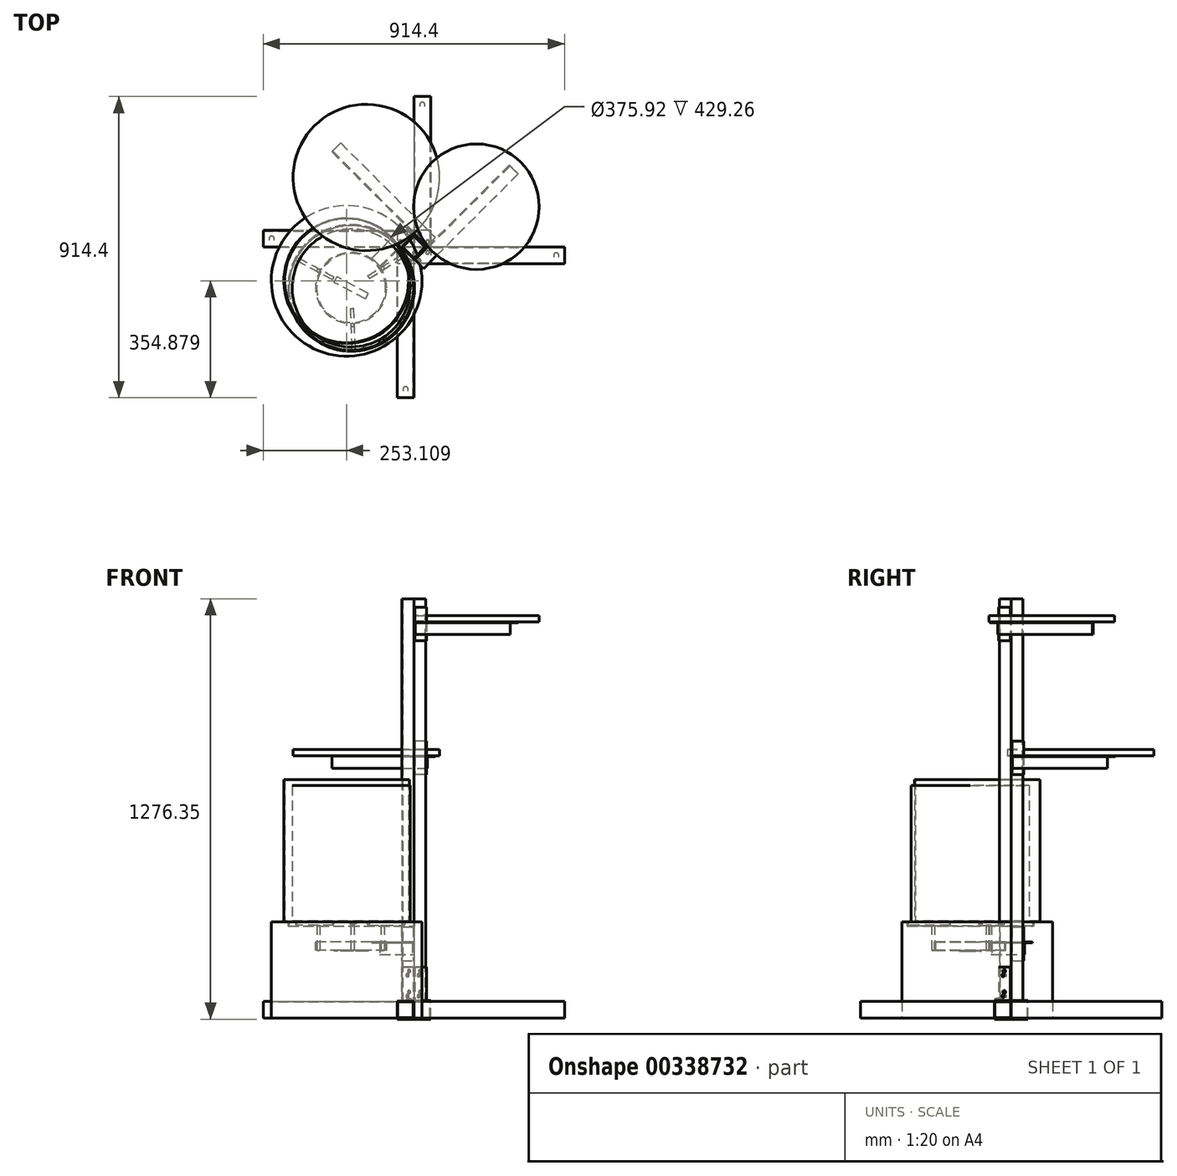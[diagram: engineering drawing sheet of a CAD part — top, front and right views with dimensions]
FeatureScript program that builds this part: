
annotation { "Feature Type Name" : "Feature", "Feature Type Description" : "" }
export const myFeature = defineFeature(function(context is Context, id is Id, definition is map)
    precondition{}
    {
        {
            var Q0;
            Q0=qCreatedBy(makeId("Front.planeOp"),FACE);
            var sketch = newSketch(context, id + "F0", { "sketchPlane" : qUnion([Q0])});
            skLineSegment(sketch, "E0.bottom", {"start": v(0, 0) * mm, "end": v(50.8, 0) * mm});
            skLineSegment(sketch, "E0.top", {"start": v(0, 50.8) * mm, "end": v(50.8, 50.8) * mm});
            skLineSegment(sketch, "E0.left", {"start": v(0, 0) * mm, "end": v(0, 50.8) * mm});
            skLineSegment(sketch, "E0.right", {"start": v(50.8, 0) * mm, "end": v(50.8, 50.8) * mm});
            skLineSegment(sketch, "E1.0", {"start": v(49.15, 1.65) * mm, "end": v(49.15, 49.15) * mm});
            skLineSegment(sketch, "E2.0", {"start": v(1.65, 49.15) * mm, "end": v(49.15, 49.15) * mm});
            skLineSegment(sketch, "E3.0", {"start": v(1.65, 1.65) * mm, "end": v(1.65, 49.15) * mm});
            skLineSegment(sketch, "E4.0", {"start": v(1.65, 1.65) * mm, "end": v(49.15, 1.65) * mm});
            skSolve(sketch);
        }
        {
            var Q0;
            Q0 = qSketchRegion(id + "F0", true);
            extrude(context, id + "F1", {"entities" : qUnion([Q0]), "oppositeDirection" : true, "depth" : 457.2 * mm});
        }
        {
            var Q0;
            Q0=makeQuery(id+"F1.opExtrude","SWEPT_FACE",FACE,{"disambiguationData":[OSD([sQuery(id+"F0.wireOp",EDGE,"E0.bottom")])]});
            var sketch = newSketch(context, id + "F2", { "sketchPlane" : qUnion([Q0])});
            skCircle(sketch, "E5", {"center": v(25.4, -431.8) * mm, "radius": 7.94 * mm});
            skSolve(sketch);
        }
        {
            var Q0;
            Q0=makeQuery(id+"F2.imprint","IMPRINT",FACE,{"disambiguationData":[TD([[makeQuery(id+"F2.imprint","IMPRINT",EDGE,{"derivedFrom":sQuery(id+"F2.wireOp",EDGE,"E5")}),1.0]])]});
            extrude(context, id + "F3", {"entities" : qUnion([Q0]), "operationType" : NewBodyOperationType.REMOVE, "endBound" : BoundingType.UP_TO_NEXT, "oppositeDirection" : true, "depth" : 25.4 * mm});
        }
        {
            var Q0;
            Q0=makeQuery(id+"F1.opExtrude","SWEPT_FACE",FACE,{"disambiguationData":[OSD([sQuery(id+"F0.wireOp",EDGE,"E0.top")])]});
            var sketch = newSketch(context, id + "F4", { "sketchPlane" : qUnion([Q0])});
            skLineSegment(sketch, "E6.bottom", {"start": v(50.8, 50.8) * mm, "end": v(-50.8, 50.8) * mm});
            skLineSegment(sketch, "E6.top", {"start": v(50.8, -50.8) * mm, "end": v(-50.8, -50.8) * mm});
            skLineSegment(sketch, "E6.left", {"start": v(50.8, 50.8) * mm, "end": v(50.8, -50.8) * mm});
            skLineSegment(sketch, "E6.right", {"start": v(-50.8, 50.8) * mm, "end": v(-50.8, -50.8) * mm});
            skSolve(sketch);
        }
        {
            var Q0;
            Q0 = qSketchRegion(id + "F4", true);
            extrude(context, id + "F5", {"entities" : qUnion([Q0]), "depth" : 3.17 * mm});
        }
        {
            var Q0;
            Q0=makeQuery(id+"F5.opExtrude","CAP_FACE",FACE,{"disambiguationData":[OSD([sQuery(id+"F4.wireOp",EDGE,"E6.bottom"),sQuery(id+"F4.wireOp",EDGE,"E6.top"),sQuery(id+"F4.wireOp",EDGE,"E6.left"),sQuery(id+"F4.wireOp",EDGE,"E6.right")])],"isStart":false});
            var sketch = newSketch(context, id + "F6", { "sketchPlane" : qUnion([Q0])});
            skLineSegment(sketch, "E7", {"start": v(-50.8, -50.8) * mm, "end": v(50.8, 50.8) * mm, "construction": true});
            skLineSegment(sketch, "E8", {"start": v(0, 0) * mm, "end": v(0, -50.8) * mm, "construction": true});
            skLineSegment(sketch, "E9", {"start": v(2.25, -38.17) * mm, "end": v(38.17, -2.25) * mm});
            skLineSegment(sketch, "E10", {"start": v(38.17, -2.25) * mm, "end": v(35.92, 0) * mm});
            skLineSegment(sketch, "E11", {"start": v(35.92, 0) * mm, "end": v(0, -35.92) * mm});
            skLineSegment(sketch, "E12", {"start": v(1.26, -37.19) * mm, "end": v(2.25, -38.17) * mm});
            skLineSegment(sketch, "E13", {"start": v(0, -35.92) * mm, "end": v(-35.92, 0) * mm});
            skLineSegment(sketch, "E14", {"start": v(-35.92, 0) * mm, "end": v(-38.17, -2.25) * mm});
            skLineSegment(sketch, "E15", {"start": v(-38.17, -2.25) * mm, "end": v(-2.19, -38.1) * mm});
            skLineSegment(sketch, "E16", {"start": v(-1.26, -37.19) * mm, "end": v(-2.19, -38.1) * mm});
            skArc(sketch, "E17", {"start": v(-1.26, -37.19) * mm, "mid": v(0, -37.7) * mm, "end": v(1.26, -37.19) * mm});
            skSolve(sketch);
        }
        {
            var Q0;
            Q0 = qSketchRegion(id + "F6", true);
            extrude(context, id + "F7", {"entities" : qUnion([Q0]), "depth" : 101.6 * mm});
        }
        {
            var Q0;
            Q0=makeQuery(id+"F5.opExtrude","CAP_FACE",FACE,{"disambiguationData":[OSD([sQuery(id+"F4.wireOp",EDGE,"E6.bottom"),sQuery(id+"F4.wireOp",EDGE,"E6.top"),sQuery(id+"F4.wireOp",EDGE,"E6.left"),sQuery(id+"F4.wireOp",EDGE,"E6.right")])],"isStart":false});
            var sketch = newSketch(context, id + "F8", { "sketchPlane" : qUnion([Q0])});
            skCircle(sketch, "E18", {"center": v(15.88, -41.27) * mm, "radius": 4.76 * mm});
            skCircle(sketch, "E19", {"center": v(41.28, -15.88) * mm, "radius": 4.76 * mm});
            skCircle(sketch, "E20.MirrorC", {"center": v(-15.88, -41.27) * mm, "radius": 4.76 * mm});
            skCircle(sketch, "E21.MirrorC", {"center": v(-41.28, -15.88) * mm, "radius": 4.76 * mm});
            skCircle(sketch, "E22.MirrorC", {"center": v(15.88, 41.27) * mm, "radius": 4.76 * mm});
            skCircle(sketch, "E23.MirrorC", {"center": v(41.28, 15.88) * mm, "radius": 4.76 * mm});
            skCircle(sketch, "E24.MirrorC", {"center": v(-15.88, 41.27) * mm, "radius": 4.76 * mm});
            skCircle(sketch, "E25.MirrorC", {"center": v(-41.28, 15.88) * mm, "radius": 4.76 * mm});
            skSolve(sketch);
        }
        {
            var Q0;
            Q0 = qSketchRegion(id + "F8", true);
            extrude(context, id + "F9", {"entities" : qUnion([Q0]), "operationType" : NewBodyOperationType.REMOVE, "oppositeDirection" : true, "depth" : 25.4 * mm});
        }
        {
            var Q0;
            Q0=makeQuery(id+"F1.opExtrude","SWEPT_FACE",FACE,{"disambiguationData":[OSD([sQuery(id+"F0.wireOp",EDGE,"E0.top")])]});
            var sketch = newSketch(context, id + "F10", { "sketchPlane" : qUnion([Q0])});
            skCircle(sketch, "E26.0", {"center": v(15.88, 41.27) * mm, "radius": 4.76 * mm, "construction": true});
            skCircle(sketch, "E27.0", {"center": v(41.28, 15.88) * mm, "radius": 4.76 * mm, "construction": true});
            skCircle(sketch, "E28", {"center": v(15.88, 41.27) * mm, "radius": 5.72 * mm});
            skCircle(sketch, "E29", {"center": v(41.28, 15.88) * mm, "radius": 5.72 * mm});
            skSolve(sketch);
        }
        {
            var Q0;
            Q0 = qSketchRegion(id + "F10", true);
            extrude(context, id + "F11", {"entities" : qUnion([Q0]), "operationType" : NewBodyOperationType.REMOVE, "endBound" : BoundingType.THROUGH_ALL, "oppositeDirection" : true, "depth" : 25.4 * mm});
        }
        {
            var Q0;
            Q0=makeQuery(id+"F1.opExtrude","SWEPT_BODY",BODY,{"disambiguationData":[OSD([sQuery(id+"F0.wireOp",EDGE,"E0.bottom"),sQuery(id+"F0.wireOp",EDGE,"E0.top"),sQuery(id+"F0.wireOp",EDGE,"E0.left"),sQuery(id+"F0.wireOp",EDGE,"E0.right"),sQuery(id+"F0.wireOp",EDGE,"E1.0"),sQuery(id+"F0.wireOp",EDGE,"E2.0"),sQuery(id+"F0.wireOp",EDGE,"E3.0"),sQuery(id+"F0.wireOp",EDGE,"E4.0")])]});
            var Q1;
            Q1=makeQuery(id+"F1.opExtrude","CAP_EDGE",EDGE,{"disambiguationData":[OSD([sQuery(id+"F0.wireOp",EDGE,"E0.left")])],"isStart":true});
            circularPattern(context, id + "F12", {"entities" : qUnion([Q0]), "axis" : qUnion([Q1]), "angle" : 360 * degree, "instanceCount" : 4, "equalSpace" : true});
        }
        {
            var Q0;
            Q0=qCreatedBy(makeId("Top.planeOp"),FACE);
            var sketch = newSketch(context, id + "F13", { "sketchPlane" : qUnion([Q0])});
            skLineSegment(sketch, "E30.0.0", {"start": v(50.8, -50.8) * mm, "end": v(50.8, 50.8) * mm});
            skLineSegment(sketch, "E30.0.1", {"start": v(50.8, 50.8) * mm, "end": v(-50.8, 50.8) * mm});
            skLineSegment(sketch, "E30.0.2", {"start": v(-50.8, 50.8) * mm, "end": v(-50.8, -50.8) * mm});
            skLineSegment(sketch, "E30.0.3", {"start": v(-50.8, -50.8) * mm, "end": v(50.8, -50.8) * mm});
            skCircle(sketch, "E31.0", {"center": v(41.28, -15.88) * mm, "radius": 4.76 * mm});
            skCircle(sketch, "E31.1", {"center": v(41.28, 15.88) * mm, "radius": 4.76 * mm});
            skCircle(sketch, "E31.2", {"center": v(15.88, -41.27) * mm, "radius": 4.76 * mm});
            skCircle(sketch, "E31.3", {"center": v(15.88, 41.27) * mm, "radius": 4.76 * mm});
            skCircle(sketch, "E31.4", {"center": v(-41.28, -15.88) * mm, "radius": 4.76 * mm});
            skCircle(sketch, "E31.5", {"center": v(-41.28, 15.88) * mm, "radius": 4.76 * mm});
            skCircle(sketch, "E31.6", {"center": v(-15.88, -41.27) * mm, "radius": 4.76 * mm});
            skCircle(sketch, "E31.7", {"center": v(-15.88, 41.27) * mm, "radius": 4.76 * mm});
            skSolve(sketch);
        }
        {
            var Q0;
            Q0 = qSketchRegion(id + "F13", true);
            extrude(context, id + "F14", {"entities" : qUnion([Q0]), "oppositeDirection" : true, "depth" : 3.17 * mm});
        }
        {
            var Q0;
            Q0=makeQuery(id+"F7.opExtrude","SWEPT_FACE",FACE,{"disambiguationData":[OSD([sQuery(id+"F6.wireOp",EDGE,"E9")])]});
            var sketch = newSketch(context, id + "F15", { "sketchPlane" : qUnion([Q0])});
            skLineSegment(sketch, "E32", {"start": v(-6.35, 176.29) * mm, "end": v(-6.35, 53.97) * mm, "construction": true});
            skLineSegment(sketch, "E33", {"start": v(0, 172.23) * mm, "end": v(0, 53.97) * mm, "construction": true});
            skCircle(sketch, "E34", {"center": v(-6.35, 66.67) * mm, "radius": 4.76 * mm});
            skCircle(sketch, "E35", {"center": v(0, 79.38) * mm, "radius": 4.76 * mm});
            skCircle(sketch, "E36", {"center": v(0, 142.88) * mm, "radius": 4.76 * mm});
            skCircle(sketch, "E37", {"center": v(-6.35, 130.18) * mm, "radius": 4.76 * mm});
            skSolve(sketch);
        }
        {
            var Q0;
            Q0 = qSketchRegion(id + "F15", true);
            extrude(context, id + "F16", {"entities" : qUnion([Q0]), "operationType" : NewBodyOperationType.REMOVE, "oppositeDirection" : true, "depth" : 25.4 * mm});
        }
        {
            var Q0;
            Q0=makeQuery(id+"F7.opExtrude","SWEPT_FACE",FACE,{"disambiguationData":[OSD([sQuery(id+"F6.wireOp",EDGE,"E15")])]});
            var sketch = newSketch(context, id + "F17", { "sketchPlane" : qUnion([Q0])});
            skLineSegment(sketch, "E38", {"start": v(6.3, 167.64) * mm, "end": v(6.3, 53.97) * mm, "construction": true});
            skPoint(sketch, "E39.endSnap0", {"position": v(-0.05, 53.97) * mm});
            skLineSegment(sketch, "E40", {"start": v(-0.05, 173.56) * mm, "end": v(-0.05, 53.97) * mm, "construction": true});
            skCircle(sketch, "E41", {"center": v(-0.05, 66.67) * mm, "radius": 4.76 * mm});
            skCircle(sketch, "E42", {"center": v(6.3, 79.38) * mm, "radius": 4.76 * mm});
            skCircle(sketch, "E43", {"center": v(6.3, 142.88) * mm, "radius": 4.76 * mm});
            skCircle(sketch, "E44", {"center": v(-0.05, 130.18) * mm, "radius": 4.76 * mm});
            skSolve(sketch);
        }
        {
            var Q0;
            Q0 = qSketchRegion(id + "F17", true);
            extrude(context, id + "F18", {"entities" : qUnion([Q0]), "operationType" : NewBodyOperationType.REMOVE, "oppositeDirection" : true, "depth" : 25.4 * mm});
        }
        {
            var Q0;
            Q0=makeQuery(id+"F5.opExtrude","CAP_FACE",FACE,{"disambiguationData":[OSD([sQuery(id+"F4.wireOp",EDGE,"E6.bottom"),sQuery(id+"F4.wireOp",EDGE,"E6.top"),sQuery(id+"F4.wireOp",EDGE,"E6.left"),sQuery(id+"F4.wireOp",EDGE,"E6.right")])],"isStart":false});
            var sketch = newSketch(context, id + "F19", { "sketchPlane" : qUnion([Q0])});
            skPoint(sketch, "E45.middle", {"position": v(0, 0) * mm});
            skLineSegment(sketch, "E46.0", {"start": v(35.92, 0) * mm, "end": v(0, -35.92) * mm});
            skLineSegment(sketch, "E46.1", {"start": v(0, -35.92) * mm, "end": v(-35.92, 0) * mm});
            skLineSegment(sketch, "E47", {"start": v(-35.92, 0) * mm, "end": v(0, 35.92) * mm});
            skLineSegment(sketch, "E48", {"start": v(0, 35.92) * mm, "end": v(35.92, 0) * mm});
            skLineSegment(sketch, "E49.0", {"start": v(-33.59, 0) * mm, "end": v(0, 33.59) * mm});
            skLineSegment(sketch, "E50.0", {"start": v(0, 33.59) * mm, "end": v(33.59, 0) * mm});
            skLineSegment(sketch, "E51.0", {"start": v(33.59, 0) * mm, "end": v(0, -33.59) * mm});
            skLineSegment(sketch, "E52.0", {"start": v(0, -33.59) * mm, "end": v(-33.59, 0) * mm});
            skSolve(sketch);
        }
        {
            var Q0;
            Q0 = qSketchRegion(id + "F19", true);
            extrude(context, id + "F20", {"entities" : qUnion([Q0]), "depth" : 1219.2 * mm});
        }
        {
            var Q0;
            Q0=makeQuery(id+"F20.opExtrude","SWEPT_FACE",FACE,{"disambiguationData":[OSD([sQuery(id+"F19.wireOp",EDGE,"E48")])]});
            var sketch = newSketch(context, id + "F21", { "sketchPlane" : qUnion([Q0])});
            skLineSegment(sketch, "E53.0", {"start": v(-25.4, 841.38) * mm, "end": v(-25.4, 739.78) * mm});
            skLineSegment(sketch, "E54.0", {"start": v(25.4, 841.38) * mm, "end": v(25.4, 739.78) * mm});
            skLineSegment(sketch, "E55", {"start": v(-25.4, 739.78) * mm, "end": v(25.4, 739.78) * mm});
            skLineSegment(sketch, "E56", {"start": v(-25.4, 841.38) * mm, "end": v(25.4, 841.38) * mm});
            skPoint(sketch, "E57.orphan", {"position": v(25.4, 1273.18) * mm});
            skPoint(sketch, "E58.orphan", {"position": v(-25.4, 1273.18) * mm});
            skPoint(sketch, "E59.orphan", {"position": v(25.4, 53.98) * mm});
            skPoint(sketch, "E60.orphan", {"position": v(-25.4, 53.98) * mm});
            skSolve(sketch);
        }
        {
            var Q0;
            Q0 = qSketchRegion(id + "F21", true);
            extrude(context, id + "F22", {"entities" : qUnion([Q0]), "depth" : 3.17 * mm});
        }
        {
            var Q0;
            Q0=makeQuery(id+"F22.opExtrude","SWEPT_FACE",FACE,{"disambiguationData":[OSD([sQuery(id+"F21.wireOp",EDGE,"E53.0")])]});
            var sketch = newSketch(context, id + "F23", { "sketchPlane" : qUnion([Q0])});
            skLineSegment(sketch, "E61.0.1", {"start": v(28.58, 796.93) * mm, "end": v(28.58, 758.83) * mm});
            skLineSegment(sketch, "E62", {"start": v(28.58, 796.93) * mm, "end": v(66.68, 796.93) * mm});
            skLineSegment(sketch, "E63", {"start": v(31.75, 829.38) * mm, "end": v(31.75, 758.83) * mm});
            skLineSegment(sketch, "E64", {"start": v(31.75, 758.83) * mm, "end": v(28.58, 758.83) * mm});
            skPoint(sketch, "E65.orphan", {"position": v(28.58, 841.38) * mm});
            skPoint(sketch, "E66.orphan", {"position": v(28.58, 739.78) * mm});
            skLineSegment(sketch, "E67", {"start": v(66.68, 796.93) * mm, "end": v(66.68, 793.75) * mm});
            skLineSegment(sketch, "E68", {"start": v(66.68, 793.75) * mm, "end": v(31.75, 793.75) * mm});
            skSolve(sketch);
        }
        {
            var Q0;
            Q0 = qSketchRegion(id + "F23", true);
            extrude(context, id + "F24", {"entities" : qUnion([Q0]), "oppositeDirection" : true, "depth" : 406.4 * mm});
        }
        {
            var Q0;
            Q0=makeQuery(id+"F24.opExtrude","SWEPT_FACE",FACE,{"disambiguationData":[OSD([sQuery(id+"F23.wireOp",EDGE,"E62")])]});
            var sketch = newSketch(context, id + "F25", { "sketchPlane" : qUnion([Q0])});
            skCircle(sketch, "E69", {"center": v(-144.13, 211.49) * mm, "radius": 222.25 * mm});
            skSolve(sketch);
        }
        {
            var Q0;
            Q0 = qSketchRegion(id + "F25", true);
            extrude(context, id + "F26", {"entities" : qUnion([Q0]), "operationType" : NewBodyOperationType.ADD, "depth" : 19.05 * mm});
        }
        {
            var Q0;
            Q0=makeQuery(id+"F5.opExtrude","CAP_FACE",FACE,{"disambiguationData":[OSD([sQuery(id+"F4.wireOp",EDGE,"E6.bottom"),sQuery(id+"F4.wireOp",EDGE,"E6.top"),sQuery(id+"F4.wireOp",EDGE,"E6.left"),sQuery(id+"F4.wireOp",EDGE,"E6.right")])],"isStart":false});
            var sketch = newSketch(context, id + "F27", { "sketchPlane" : qUnion([Q0])});
            skCircle(sketch, "E70.0", {"center": v(-15.88, -41.27) * mm, "radius": 4.76 * mm, "construction": true});
            skCircle(sketch, "E71.cCircle", {"center": v(-15.88, -41.27) * mm, "radius": 7.14 * mm, "construction": true});
            skLineSegment(sketch, "E71.0", {"start": v(-8.73, -37.15) * mm, "end": v(-8.73, -45.4) * mm});
            skLineSegment(sketch, "E71.1", {"start": v(-8.73, -45.4) * mm, "end": v(-15.88, -49.52) * mm});
            skLineSegment(sketch, "E71.2", {"start": v(-15.87, -49.52) * mm, "end": v(-23.02, -45.4) * mm});
            skLineSegment(sketch, "E71.3", {"start": v(-23.02, -45.4) * mm, "end": v(-23.02, -37.15) * mm});
            skLineSegment(sketch, "E71.4", {"start": v(-23.02, -37.15) * mm, "end": v(-15.87, -33.03) * mm});
            skLineSegment(sketch, "E71.5", {"start": v(-15.88, -33.03) * mm, "end": v(-8.73, -37.15) * mm});
            skPoint(sketch, "E71.0.midPoint", {"position": v(-8.73, -41.27) * mm});
            skSolve(sketch);
        }
        {
            var Q0;
            Q0 = qSketchRegion(id + "F27", true);
            extrude(context, id + "F28", {"entities" : qUnion([Q0]), "depth" : 6.35 * mm});
        }
        {
            var Q0;
            Q0=makeQuery(id+"F20.opExtrude","SWEPT_FACE",FACE,{"disambiguationData":[OSD([sQuery(id+"F19.wireOp",EDGE,"E46.0")])]});
            var sketch = newSketch(context, id + "F29", { "sketchPlane" : qUnion([Q0])});
            skLineSegment(sketch, "E72.0", {"start": v(-25.4, 1247.77) * mm, "end": v(-25.4, 1146.17) * mm});
            skLineSegment(sketch, "E73", {"start": v(-25.4, 1146.17) * mm, "end": v(25.4, 1146.17) * mm});
            skLineSegment(sketch, "E74", {"start": v(-25.4, 1247.77) * mm, "end": v(25.4, 1247.77) * mm});
            skPoint(sketch, "E75.orphan", {"position": v(-25.4, 1273.18) * mm});
            skPoint(sketch, "E76.orphan", {"position": v(-25.4, 53.98) * mm});
            skLineSegment(sketch, "E77", {"start": v(25.4, 1247.77) * mm, "end": v(25.4, 1146.17) * mm});
            skSolve(sketch);
        }
        {
            var Q0;
            Q0 = qSketchRegion(id + "F29", true);
            extrude(context, id + "F30", {"entities" : qUnion([Q0]), "depth" : 3.17 * mm});
        }
        {
            var Q0;
            Q0=makeQuery(id+"F30.opExtrude","SWEPT_FACE",FACE,{"disambiguationData":[OSD([sQuery(id+"F29.wireOp",EDGE,"E72.0")])]});
            var sketch = newSketch(context, id + "F31", { "sketchPlane" : qUnion([Q0])});
            skLineSegment(sketch, "E78.0", {"start": v(28.57, 1203.33) * mm, "end": v(28.57, 1165.22) * mm});
            skLineSegment(sketch, "E79", {"start": v(28.57, 1203.33) * mm, "end": v(66.67, 1203.33) * mm});
            skLineSegment(sketch, "E80", {"start": v(66.67, 1203.33) * mm, "end": v(66.67, 1200.15) * mm});
            skLineSegment(sketch, "E81", {"start": v(66.67, 1200.15) * mm, "end": v(31.75, 1200.15) * mm});
            skLineSegment(sketch, "E82", {"start": v(31.75, 1200.15) * mm, "end": v(31.75, 1165.22) * mm});
            skLineSegment(sketch, "E83", {"start": v(31.75, 1165.22) * mm, "end": v(28.57, 1165.22) * mm});
            skPoint(sketch, "E84.orphan", {"position": v(28.57, 1146.17) * mm});
            skPoint(sketch, "E85.orphan", {"position": v(28.57, 1247.77) * mm});
            skSolve(sketch);
        }
        {
            var Q0;
            Q0 = qSketchRegion(id + "F31", true);
            extrude(context, id + "F32", {"entities" : qUnion([Q0]), "oppositeDirection" : true, "depth" : 406.4 * mm});
        }
        {
            var Q0;
            Q0=makeQuery(id+"F32.opExtrude","SWEPT_FACE",FACE,{"disambiguationData":[OSD([sQuery(id+"F31.wireOp",EDGE,"E79")])]});
            var sketch = newSketch(context, id + "F33", { "sketchPlane" : qUnion([Q0])});
            skCircle(sketch, "E86", {"center": v(189.77, 122.9) * mm, "radius": 190.5 * mm});
            skSolve(sketch);
        }
        {
            var Q0;
            Q0 = qSketchRegion(id + "F33", true);
            extrude(context, id + "F34", {"entities" : qUnion([Q0]), "depth" : 19.05 * mm});
        }
        {
            var Q0;
            Q0=makeQuery(id+"F12.opPattern","COPY",FACE,{"derivedFrom":makeQuery(id+"F1.opExtrude","SWEPT_FACE",FACE,{"disambiguationData":[OSD([sQuery(id+"F0.wireOp",EDGE,"E0.bottom")])]}),"instanceName":"1"});
            var sketch = newSketch(context, id + "F35", { "sketchPlane" : qUnion([Q0])});
            skCircle(sketch, "E87", {"center": v(-204.1, 102.32) * mm, "radius": 228.6 * mm});
            skSolve(sketch);
        }
        {
            var Q0;
            Q0 = qSketchRegion(id + "F35", true);
            extrude(context, id + "F36", {"entities" : qUnion([Q0]), "oppositeDirection" : true, "depth" : 292.1 * mm});
        }
        {
            var Q0;
            Q0=makeQuery(id+"F36.opExtrude","CAP_FACE",FACE,{"disambiguationData":[OSD([sQuery(id+"F35.wireOp",EDGE,"E87")])],"isStart":false});
            var sketch = newSketch(context, id + "F37", { "sketchPlane" : qUnion([Q0])});
            skCircle(sketch, "E88.0", {"center": v(-204.1, -102.32) * mm, "radius": 228.6 * mm, "construction": true});
            skCircle(sketch, "E89", {"center": v(-204.1, -102.32) * mm, "radius": 190.5 * mm});
            skSolve(sketch);
        }
        {
            var Q0;
            Q0 = qSketchRegion(id + "F37", true);
            extrude(context, id + "F38", {"entities" : qUnion([Q0]), "depth" : 431.8 * mm});
        }
        {
            var Q0;
            Q0=makeQuery(id+"F38.opExtrude","CAP_FACE",FACE,{"disambiguationData":[OSD([sQuery(id+"F37.wireOp",EDGE,"E89")])],"isStart":false});
            shell(context, id + "F39", {"entities" : qUnion([Q0]), "thickness" : 2.54 * mm});
        }
        {
            var Q0;
            Q0=makeQuery(id+"F20.opExtrude","SWEPT_FACE",FACE,{"disambiguationData":[OSD([sQuery(id+"F19.wireOp",EDGE,"E47")])]});
            var sketch = newSketch(context, id + "F40", { "sketchPlane" : qUnion([Q0])});
            skLineSegment(sketch, "E90", {"start": v(-25.4, 276.23) * mm, "end": v(25.4, 276.23) * mm});
            skLineSegment(sketch, "E91", {"start": v(25.4, 276.23) * mm, "end": v(25.4, 174.62) * mm});
            skLineSegment(sketch, "E92", {"start": v(25.4, 174.62) * mm, "end": v(-25.4, 174.62) * mm});
            skLineSegment(sketch, "E93", {"start": v(-25.4, 174.63) * mm, "end": v(-25.4, 276.23) * mm});
            skSolve(sketch);
        }
        {
            var Q0;
            Q0 = qSketchRegion(id + "F40", true);
            extrude(context, id + "F41", {"entities" : qUnion([Q0]), "depth" : 3.17 * mm});
        }
        {
            var Q0;
            Q0=makeQuery(id+"F41.opExtrude","SWEPT_FACE",FACE,{"disambiguationData":[OSD([sQuery(id+"F40.wireOp",EDGE,"E93")])]});
            var sketch = newSketch(context, id + "F42", { "sketchPlane" : qUnion([Q0])});
            skLineSegment(sketch, "E94", {"start": v(28.58, 231.78) * mm, "end": v(66.68, 231.78) * mm});
            skLineSegment(sketch, "E95", {"start": v(66.68, 231.78) * mm, "end": v(66.68, 228.6) * mm});
            skLineSegment(sketch, "E96", {"start": v(66.68, 228.6) * mm, "end": v(31.75, 228.6) * mm});
            skLineSegment(sketch, "E97", {"start": v(31.75, 228.6) * mm, "end": v(31.75, 193.68) * mm});
            skLineSegment(sketch, "E98", {"start": v(31.75, 193.68) * mm, "end": v(28.58, 193.68) * mm});
            skLineSegment(sketch, "E99.0", {"start": v(28.58, 231.78) * mm, "end": v(28.58, 193.68) * mm});
            skPoint(sketch, "E100.orphan", {"position": v(28.58, 174.63) * mm});
            skPoint(sketch, "E101.orphan", {"position": v(28.58, 276.23) * mm});
            skSolve(sketch);
        }
        {
            var Q0;
            Q0 = qSketchRegion(id + "F42", true);
            extrude(context, id + "F43", {"entities" : qUnion([Q0]), "oppositeDirection" : true, "depth" : 139.7 * mm});
        }
        {
            var Q0;
            Q0=makeQuery(id+"F43.opExtrude","SWEPT_FACE",FACE,{"disambiguationData":[OSD([sQuery(id+"F42.wireOp",EDGE,"E94")])]});
            var sketch = newSketch(context, id + "F44", { "sketchPlane" : qUnion([Q0])});
            skCircle(sketch, "E102", {"center": v(-190.4, -123.92) * mm, "radius": 107.95 * mm});
            skCircle(sketch, "E103.0", {"center": v(-190.4, -123.92) * mm, "radius": 104.78 * mm});
            skSolve(sketch);
        }
        {
            var Q0;
            Q0 = qSketchRegion(id + "F44", true);
            extrude(context, id + "F45", {"entities" : qUnion([Q0]), "oppositeDirection" : true, "depth" : 25.4 * mm});
        }
        {
            var Q0;
            Q0=makeQuery(id+"F45.opExtrude","CAP_FACE",FACE,{"disambiguationData":[OSD([sQuery(id+"F44.wireOp",EDGE,"E102"),sQuery(id+"F44.wireOp",EDGE,"E103.0")])],"isStart":false});
            var sketch = newSketch(context, id + "F46", { "sketchPlane" : qUnion([Q0])});
            skCircle(sketch, "E104.0", {"center": v(-190.4, 123.92) * mm, "radius": 107.95 * mm, "construction": true});
            skLineSegment(sketch, "E105", {"start": v(-190.4, 123.92) * mm, "end": v(-82.48, 56.49) * mm, "construction": true});
            skCircle(sketch, "E106", {"center": v(-94.8, 64.19) * mm, "radius": 4.76 * mm});
            skLineSegment(sketch, "E107", {"start": v(-190.4, 123.92) * mm, "end": v(-185.68, 258.68) * mm, "construction": true});
            skLineSegment(sketch, "E108", {"start": v(-190.4, 123.92) * mm, "end": v(-299.59, 65.86) * mm, "construction": true});
            skCircle(sketch, "E109", {"center": v(-186.46, 236.56) * mm, "radius": 4.76 * mm});
            skCircle(sketch, "E110", {"center": v(-289.9, 71) * mm, "radius": 4.76 * mm});
            skLineSegment(sketch, "E111", {"start": v(-190.4, 123.92) * mm, "end": v(-190.4, 55.36) * mm, "construction": true});
            skSolve(sketch);
        }
        {
            var Q0;
            Q0 = qSketchRegion(id + "F46", true);
            extrude(context, id + "F47", {"entities" : qUnion([Q0]), "oppositeDirection" : true, "depth" : 76.2 * mm});
        }
        {
            var Q0;
            Q0=makeQuery(id+"F47.opExtrude","CAP_FACE",FACE,{"disambiguationData":[OSD([sQuery(id+"F46.wireOp",EDGE,"E110")])],"isStart":false});
            var sketch = newSketch(context, id + "F48", { "sketchPlane" : qUnion([Q0])});
            skLineSegment(sketch, "E112", {"start": v(-289.9, -71) * mm, "end": v(-295.33, -81.2) * mm});
            skCircle(sketch, "E113.0.0", {"center": v(-94.8, -64.19) * mm, "radius": 4.76 * mm, "construction": true});
            skCircle(sketch, "E114.0.0", {"center": v(-186.46, -236.56) * mm, "radius": 4.76 * mm, "construction": true});
            skCircle(sketch, "E115.0", {"center": v(-190.4, -123.92) * mm, "radius": 107.95 * mm, "construction": true});
            skLineSegment(sketch, "E116", {"start": v(-190.4, -123.92) * mm, "end": v(-289.9, -71) * mm, "construction": true});
            skLineSegment(sketch, "E117", {"start": v(-190.4, -123.92) * mm, "end": v(-186.46, -236.56) * mm, "construction": true});
            skLineSegment(sketch, "E118", {"start": v(-190.4, -123.92) * mm, "end": v(-94.8, -64.19) * mm, "construction": true});
            skLineSegment(sketch, "E119", {"start": v(-186.46, -236.56) * mm, "end": v(-173.8, -236.12) * mm});
            skLineSegment(sketch, "E120", {"start": v(-94.8, -64.19) * mm, "end": v(-88.44, -74.37) * mm});
            skSolve(sketch);
        }
        {
            var Q0;
            Q0=sQuery(id+"F48.wireOp",EDGE,"E112");
            cPlane(context, id + "F49", {"entities" : qUnion([Q0]), "cplaneType" : CPlaneType.LINE_ANGLE, "offset" : 25.4 * mm, "angle" : 90 * degree, "width" : 152.4 * mm, "height" : 152.4 * mm});
        }
        {
            var Q0;
            Q0=qCreatedBy(id+"F49.planeOp",FACE);
            var sketch = newSketch(context, id + "F50", { "sketchPlane" : qUnion([Q0])});
            skLineSegment(sketch, "E121.0", {"start": v(-198.8, 282.58) * mm, "end": v(-210.35, 282.58) * mm, "construction": true});
            skCircle(sketch, "E122", {"center": v(-198.8, 287.34) * mm, "radius": 4.76 * mm});
            skSolve(sketch);
        }
        {
            var Q0;
            Q0 = qSketchRegion(id + "F50", true);
            extrude(context, id + "F51", {"entities" : qUnion([Q0]), "depth" : 50.8 * mm, "hasSecondDirection" : true, "secondDirectionOppositeDirection" : true, "secondDirectionDepth" : 76.2 * mm});
        }
        {
            var Q0;
            Q0=sQuery(id+"F48.wireOp",EDGE,"E119");
            cPlane(context, id + "F52", {"entities" : qUnion([Q0]), "cplaneType" : CPlaneType.LINE_ANGLE, "offset" : 25.4 * mm, "angle" : 0 * degree, "width" : 152.4 * mm, "height" : 152.4 * mm});
        }
        {
            var Q0;
            Q0=sQuery(id+"F48.wireOp",EDGE,"E120");
            cPlane(context, id + "F53", {"entities" : qUnion([Q0]), "cplaneType" : CPlaneType.LINE_ANGLE, "offset" : 25.4 * mm, "angle" : 90 * degree, "width" : 152.4 * mm, "height" : 152.4 * mm});
        }
        {
            var Q0;
            Q0=qCreatedBy(id+"F53.planeOp",FACE);
            var sketch = newSketch(context, id + "F54", { "sketchPlane" : qUnion([Q0])});
            skLineSegment(sketch, "E123.0", {"start": v(-4.2, 282.58) * mm, "end": v(-16.2, 282.58) * mm, "construction": true});
            skCircle(sketch, "E124", {"center": v(-4.2, 287.34) * mm, "radius": 4.76 * mm});
            skSolve(sketch);
        }
        {
            var Q0;
            Q0 = qSketchRegion(id + "F54", true);
            extrude(context, id + "F55", {"entities" : qUnion([Q0]), "oppositeDirection" : true, "depth" : 50.8 * mm, "hasSecondDirection" : true, "secondDirectionOppositeDirection" : false, "secondDirectionDepth" : 76.2 * mm});
        }
        {
            var Q0;
            Q0=qCreatedBy(id+"F52.planeOp",FACE);
            var sketch = newSketch(context, id + "F56", { "sketchPlane" : qUnion([Q0])});
            skLineSegment(sketch, "E125.0", {"start": v(194.6, 282.58) * mm, "end": v(181.93, 282.58) * mm, "construction": true});
            skCircle(sketch, "E126", {"center": v(194.6, 287.34) * mm, "radius": 4.76 * mm});
            skSolve(sketch);
        }
        {
            var Q0;
            Q0 = qSketchRegion(id + "F56", true);
            extrude(context, id + "F57", {"entities" : qUnion([Q0]), "depth" : 50.8 * mm, "hasSecondDirection" : true, "secondDirectionOppositeDirection" : true, "secondDirectionDepth" : 76.2 * mm});
        }
        {
            var Q0;
            Q0=sQuery(id+"F48.wireOp",VERTEX,"E118.start");
            var Q1;
            Q1=qCreatedBy(id+"F49.planeOp",FACE);
            cPlane(context, id + "F58", {"entities" : qUnion([Q0, Q1]), "cplaneType" : CPlaneType.PLANE_POINT, "offset" : 25.4 * mm, "width" : 152.4 * mm, "height" : 152.4 * mm});
        }
        {
            var Q0;
            Q0=qCreatedBy(id+"F58.planeOp",FACE);
            var sketch = newSketch(context, id + "F59", { "sketchPlane" : qUnion([Q0])});
            skLineSegment(sketch, "E127", {"start": v(-198.8, 282.58) * mm, "end": v(-198.8, 308.13) * mm, "construction": true});
            skSolve(sketch);
        }
        {
            var Q0;
            Q0=makeQuery(id+"F57.opExtrude","CAP_FACE",FACE,{"disambiguationData":[OSD([sQuery(id+"F56.wireOp",EDGE,"E126")])],"isStart":true});
            var sketch = newSketch(context, id + "F60", { "sketchPlane" : qUnion([Q0])});
            skLineSegment(sketch, "E128.bottom", {"start": v(-186.48, 300.04) * mm, "end": v(-185.4, 300.04) * mm});
            skLineSegment(sketch, "E128.top", {"start": v(-186.48, 287.08) * mm, "end": v(-185.4, 287.08) * mm});
            skLineSegment(sketch, "E128.left", {"start": v(-186.48, 300.04) * mm, "end": v(-186.48, 287.08) * mm});
            skLineSegment(sketch, "E128.right", {"start": v(-185.4, 300.04) * mm, "end": v(-185.4, 287.08) * mm});
            skSolve(sketch);
        }
        {
            var Q0;
            Q0 = qSketchRegion(id + "F60", true);
            extrude(context, id + "F61", {"entities" : qUnion([Q0]), "operationType" : NewBodyOperationType.REMOVE, "oppositeDirection" : true, "depth" : 0.03 * mm});
        }
        {
            var Q0;
            Q0=makeQuery(id+"F57.opExtrude","CAP_FACE",FACE,{"disambiguationData":[OSD([sQuery(id+"F56.wireOp",EDGE,"E126")])],"isStart":true});
            var sketch = newSketch(context, id + "F62", { "sketchPlane" : qUnion([Q0])});
            skLineSegment(sketch, "E129", {"start": v(-194.6, 287.34) * mm, "end": v(-194.6, 301.9) * mm});
            skSolve(sketch);
        }
        {
            var Q0;
            Q0=sQuery(id+"F62.wireOp",EDGE,"E129");
            cPlane(context, id + "F63", {"entities" : qUnion([Q0]), "cplaneType" : CPlaneType.LINE_ANGLE, "offset" : 25.4 * mm, "angle" : 0 * degree, "width" : 152.4 * mm, "height" : 152.4 * mm});
        }
        {
            var Q0;
            Q0=qCreatedBy(id+"F63.planeOp",FACE);
            var sketch = newSketch(context, id + "F64", { "sketchPlane" : qUnion([Q0])});
            skLineSegment(sketch, "E130.0", {"start": v(-312.72, 287.34) * mm, "end": v(-312.72, 301.9) * mm, "construction": true});
            skLineSegment(sketch, "E131", {"start": v(-312.72, 287.34) * mm, "end": v(-315.9, 287.34) * mm, "construction": true});
            skLineSegment(sketch, "E132", {"start": v(-315.9, 279.4) * mm, "end": v(-315.9, 292.1) * mm});
            skLineSegment(sketch, "E133", {"start": v(-315.9, 292.1) * mm, "end": v(-312.72, 292.1) * mm});
            skLineSegment(sketch, "E134", {"start": v(-312.72, 292.1) * mm, "end": v(-312.72, 279.4) * mm});
            skLineSegment(sketch, "E135", {"start": v(-312.72, 279.4) * mm, "end": v(-315.9, 279.4) * mm});
            skSolve(sketch);
        }
        {
            var Q0;
            Q0 = qSketchRegion(id + "F64", true);
            var Q1;
            Q1=sQuery(id+"F59.wireOp",EDGE,"E127");
            revolve(context, id + "F65", {"entities" : qUnion([Q0]), "axis" : qUnion([Q1]), "revolveType" : RevolveType.FULL});
        }
        {
            var Q0;
            Q0=qCreatedBy(id+"F58.planeOp",FACE);
            var sketch = newSketch(context, id + "F66", { "sketchPlane" : qUnion([Q0])});
            skLineSegment(sketch, "E136.0", {"start": v(-208.32, 206.38) * mm, "end": v(-189.27, 206.38) * mm});
            skLineSegment(sketch, "E137", {"start": v(-189.27, 203.2) * mm, "end": v(-189.27, 206.38) * mm});
            skLineSegment(sketch, "E138", {"start": v(-189.27, 203.2) * mm, "end": v(-208.32, 203.2) * mm});
            skLineSegment(sketch, "E139", {"start": v(-208.32, 206.38) * mm, "end": v(-208.32, 203.2) * mm});
            skLineSegment(sketch, "E140", {"start": v(-198.8, 206.38) * mm, "end": v(-198.8, 156.1) * mm, "construction": true});
            skPoint(sketch, "E141.orphan", {"position": v(-90.85, 206.38) * mm});
            skPoint(sketch, "E142.orphan", {"position": v(-306.75, 206.38) * mm});
            skSolve(sketch);
        }
        {
            var Q0;
            Q0 = qSketchRegion(id + "F66", true);
            extrude(context, id + "F67", {"entities" : qUnion([Q0]), "depth" : 53.97 * mm, "hasSecondDirection" : true, "secondDirectionOppositeDirection" : true, "secondDirectionDepth" : 53.97 * mm});
        }
        {
            var Q0;
            Q0=makeQuery(id+"F65.opRevolve","SWEPT_FACE",FACE,{"disambiguationData":[OSD([sQuery(id+"F64.wireOp",EDGE,"E133")])]});
            var sketch = newSketch(context, id + "F68", { "sketchPlane" : qUnion([Q0])});
            skCircle(sketch, "E143", {"center": v(-190.4, -123.92) * mm, "radius": 179.07 * mm});
            skSolve(sketch);
        }
        {
            var Q0;
            Q0 = qSketchRegion(id + "F68", true);
            extrude(context, id + "F69", {"entities" : qUnion([Q0]), "depth" : 414.02 * mm});
        }
    });
